# Revit family: FS12T-66
name_source: partatom
category: Communication Devices
revit_build: Autodesk Revit 2014 (Build: 20140709_2115(x64)
units: mm (PartAtom-declared; Revit-internal decimal feet)

## types (1)
- Full-Range, Outdoor, Horn Loudspeaker
    100V Taps = 200W, 100W, 50W
    70V Taps = 400W, 200W, 100W, 50W
    Baffle Material = <By Category>
    Body Material = Default
    Color = <By Category>
    Cost = 865.99 $
    Cost MSRP = 865.99 $
    Coverage Horizontal = 60.00°
    Coverage Vertical = 60.00°
    Depth = 19.6 "
    Description = 12" 2-WAY MULTIPURPOSE HORN LOUDSPEAKER SYSTEM 60° X 60°
    Dispersion Angle = 60.00°
    Enclosure Material = <By Category>
    Environmental Testing = MIL-DTL-12606
    Family Code (default) = LOUD SPEAKERS
    Frequency Response  = 80Hz - 17.6kHz
    Grill Material = QF_Plastic - Black - Fine Textured
    Height = 18.49 "
    IQ Category = SPEAKERS
    Impedance = 8
    Ingress Protection = IP45 When Tilted 5° Downwards
    Input Connectors = Barrier Terminal
    Manufacturer = ATLAS SOUND
    Manufacturer URL = https://www.atlasied.com
    Market = Commercial, Higher Education, Emergency
    MasterFormat = 27 41 13
    MaterFormat Title = SPEAKERS
    Max Input Ratings (8Ω) = 400 W Continuous, 800 W Program
    Maximum Output = 128.5 dB
    Model = FS12T-66
    Mount Material = QF_Plastic - Black - Fine Textured
    Mounting/Rigging Provisions = 6mm Stainless Steel U-Bracket
    OmniClass Number = 23-37 17 13 19
    OmniClass Title = SPEAKERS
    Operation Mode = Non-Powered Passive
    Pitch = 0.00°
    Power Rating (RMS) = 400 watts RMS
    Product Documentation Link = https://www.atlasied.com
    Product Page URL = https://www.atlasied.com
    Recommended Power Amplification = 400W @ 4Ω
    Recommended Signal Processing = 70 Hz High Pass Filter
    Rotation = 0.00°
    SPL Max = 128.5
    ScheduleType |RF| = AtlasIED Master
    Sensitivity = 102.5
    Speaker Dispersion = 60.00°
    Splay Angle Maximum = 0.00°
    Transformer Option = Yes
    URL = www.atlassound.com
    Vertical Symmetry = Yes
    Warranty = 5 Year
    Weight Product = 48
    Width = 19.6 "

## geometry (parser evidence)
native form markers: Blend x6, Sweep x4
no freeform markers — native parametric forms only
